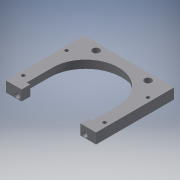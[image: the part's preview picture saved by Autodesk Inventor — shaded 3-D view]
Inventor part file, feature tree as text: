
AUTODESK INVENTOR PART (.ipt)
format: ipt  version: 2017 (Build 210142000, 142)  size: 188,928 bytes
history: native  units: mm
features: extrude x5, sketch x5, projected_geometry x2, reference x2, other x2, mirror x1
ambient origin geometry x8: Origin, YZ Plane, XZ Plane, XY Plane, X Axis, Y Axis, Z Axis, Center Point
bodies: Solid1 (feature_tree)
feature tree (17):
  extrude  "Extrusion1"  Depth=80.0mm
  extrude  "Extrusion2"  Depth=2.0mm
  extrude  "Extrusion3"  Depth=10.0mm
  extrude  "Extrusion4"  Depth=5.0mm TaperAngle=0.0deg
  extrude  "Extrusion5"  Depth=4.0mm
  mirror  "Mirror1"
  sketch  "Sketch1"  dims[d0=8.0mm d1=80.0mm]
  sketch  "Sketch2"  dims[d2=2.0mm d3=50.0mm]
  projected_geometry  "Projected Loop1"
  sketch  "Sketch3"  dims[d4=10.0mm d5=40.0mm]
  sketch  "Sketch4"  dims[d6=7.0mm d7=0.0mm d9=5.0mm d10=0.0mm]
  reference  "Reference1"
  reference  "Reference2"
  sketch  "Sketch5"  dims[d11=76.0mm d12=4.0mm d13=5.0mm d14=50.0mm d15=4.0mm d16=0.0mm d17=10.0mm d18=0.0mm d19=6.0mm d20=4.0mm d21=10.0mm d22=0.0mm]
  projected_geometry  "Projected Loop2"
  other  "peristaltic pump.iam"
  other  "frame bottom:1"
